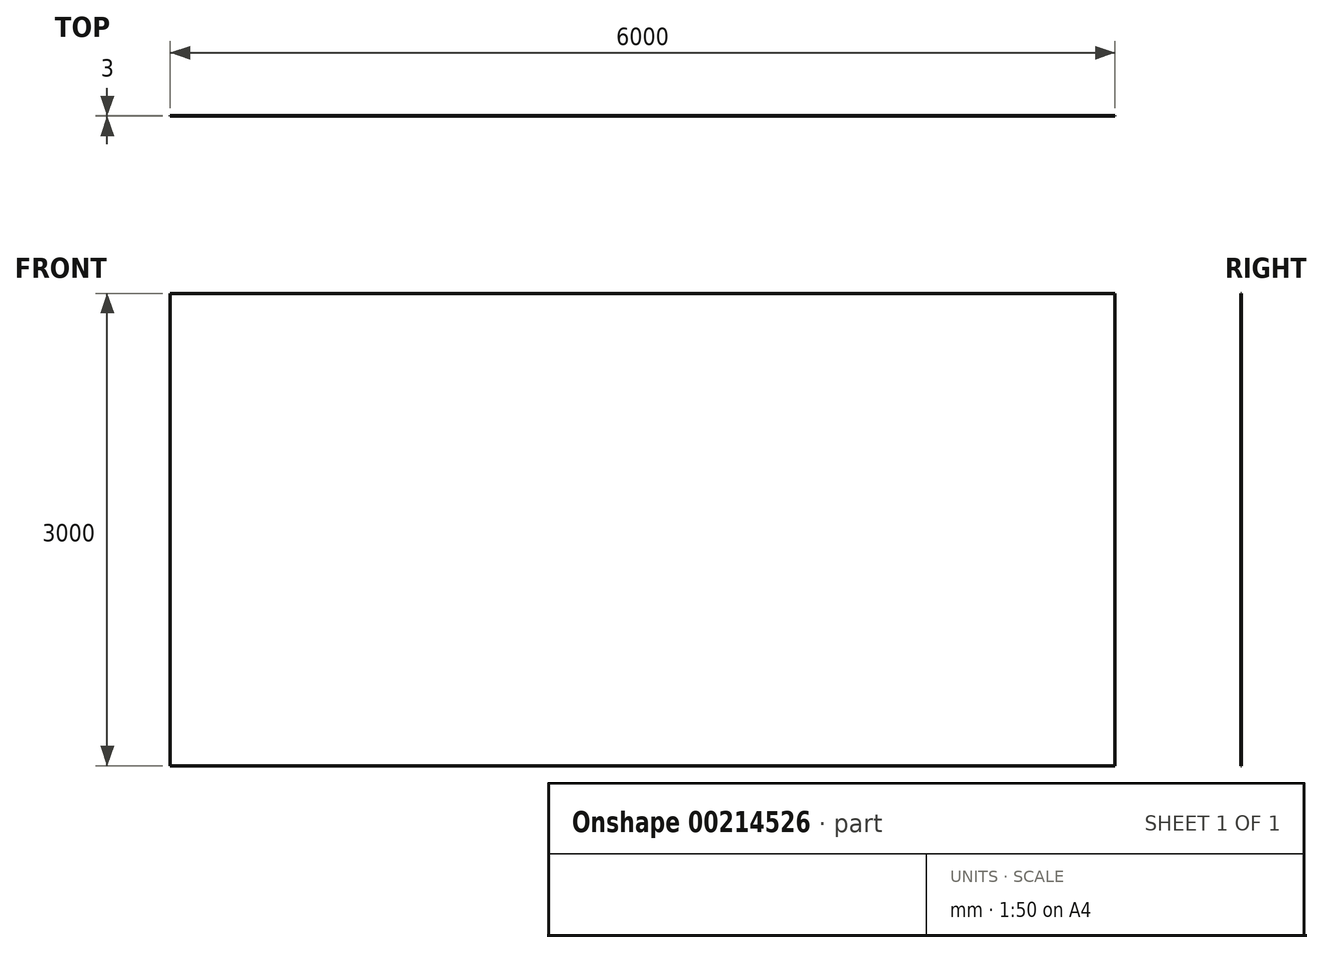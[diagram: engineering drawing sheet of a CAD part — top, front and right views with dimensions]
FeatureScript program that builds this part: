
annotation { "Feature Type Name" : "Feature", "Feature Type Description" : "" }
export const myFeature = defineFeature(function(context is Context, id is Id, definition is map)
    precondition{}
    {
        {
            var Q0;
            Q0=qCreatedBy(makeId("Front.planeOp"),FACE);
            var sketch = newSketch(context, id + "F0", { "sketchPlane" : qUnion([Q0])});
            skLineSegment(sketch, "E0.bottom", {"start": v(-3000, 1500) * mm, "end": v(3000, 1500) * mm});
            skLineSegment(sketch, "E0.top", {"start": v(-3000, -1500) * mm, "end": v(3000, -1500) * mm});
            skLineSegment(sketch, "E0.left", {"start": v(-3000, 1500) * mm, "end": v(-3000, -1500) * mm});
            skLineSegment(sketch, "E0.right", {"start": v(3000, 1500) * mm, "end": v(3000, -1500) * mm});
            skSolve(sketch);
        }
        {
            var Q0;
            Q0 = qSketchRegion(id + "F0", true);
            extrude(context, id + "F1", {"entities" : qUnion([Q0]), "depth" : 3 * mm});
        }
    });
